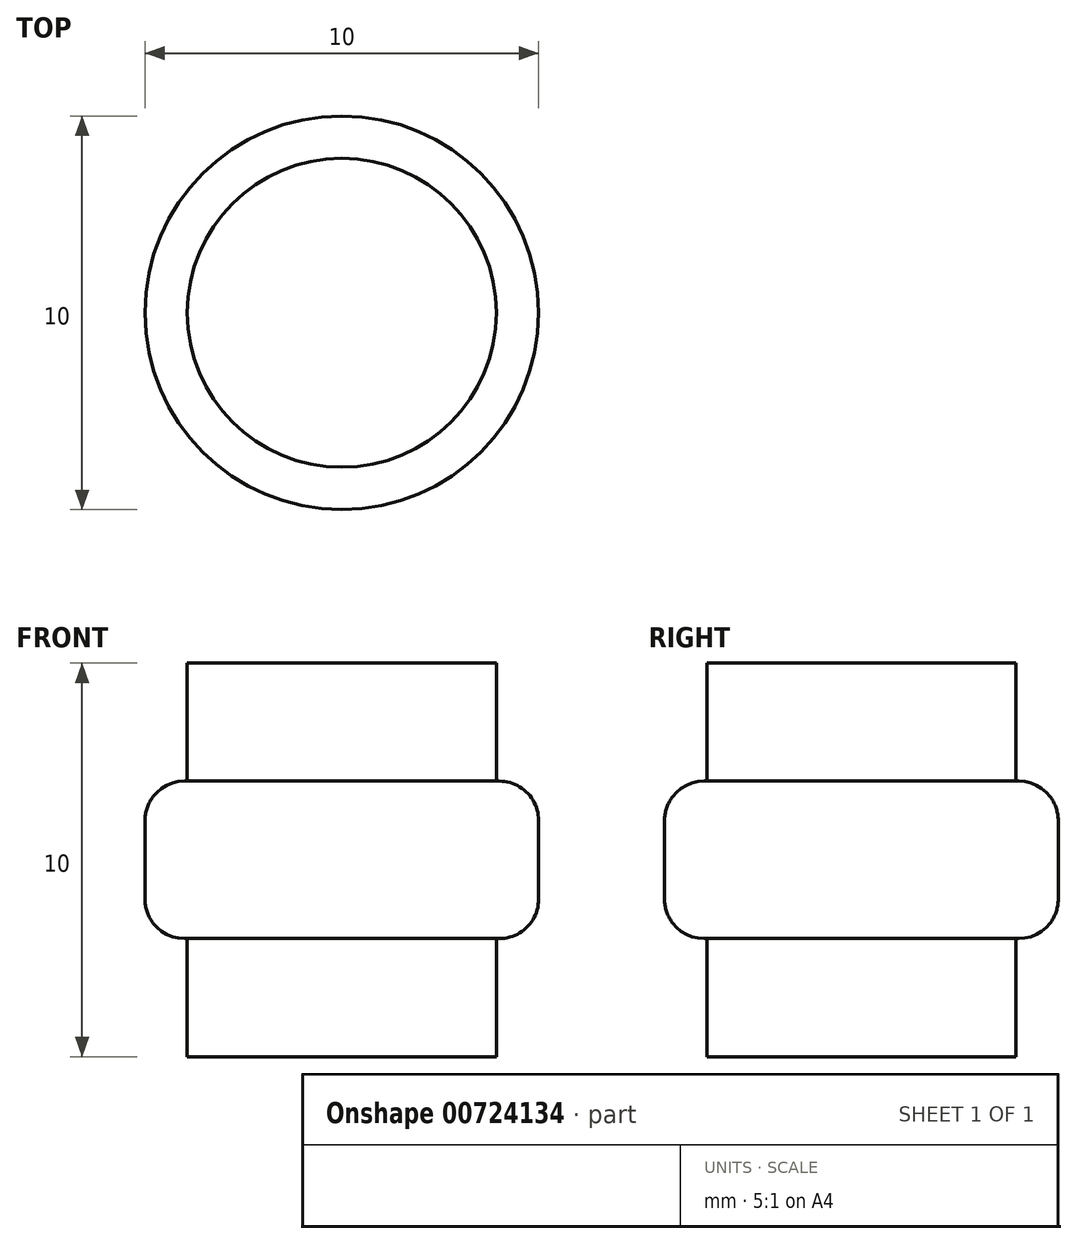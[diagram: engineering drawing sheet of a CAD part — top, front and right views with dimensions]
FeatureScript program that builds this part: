
annotation { "Feature Type Name" : "Feature", "Feature Type Description" : "" }
export const myFeature = defineFeature(function(context is Context, id is Id, definition is map)
    precondition{}
    {
        {
            var Q0;
            Q0=qCreatedBy(makeId("Top.planeOp"),FACE);
            var sketch = newSketch(context, id + "F0", { "sketchPlane" : qUnion([Q0])});
            skCircle(sketch, "E0", {"center": v(0, 0) * mm, "radius": 3.93 * mm});
            skCircle(sketch, "E1", {"center": v(0, 0) * mm, "radius": 5 * mm});
            skSolve(sketch);
        }
        {
            var Q0;
            Q0=makeQuery(id+"F0.imprint","IMPRINT",FACE,{"disambiguationData":[TD([[makeQuery(id+"F0.imprint","IMPRINT",EDGE,{"derivedFrom":sQuery(id+"F0.wireOp",EDGE,"E0")}),1.0]])]});
            extrude(context, id + "F1", {"entities" : qUnion([Q0]), "endBound" : BoundingType.SYMMETRIC, "oppositeDirection" : true, "depth" : 10 * mm, "offsetDistance" : 25 * mm});
        }
        {
            var Q0;
            Q0=makeQuery(id+"F0.imprint","IMPRINT",FACE,{"disambiguationData":[TD([[makeQuery(id+"F0.imprint","IMPRINT",EDGE,{"derivedFrom":sQuery(id+"F0.wireOp",EDGE,"E0")}),-1.0]])]});
            extrude(context, id + "F2", {"entities" : qUnion([Q0]), "operationType" : NewBodyOperationType.ADD, "endBound" : BoundingType.SYMMETRIC, "depth" : 4 * mm, "offsetDistance" : 25 * mm});
        }
        {
            var Q0;
            Q0=makeQuery(id+"F2.opExtrude","CAP_EDGE",EDGE,{"disambiguationData":[OSD([sQuery(id+"F0.wireOp",EDGE,"E1")])],"isStart":false});
            var Q1;
            Q1=makeQuery(id+"F2.opExtrude","CAP_EDGE",EDGE,{"disambiguationData":[OSD([sQuery(id+"F0.wireOp",EDGE,"E1")])],"isStart":true});
            fillet(context, id + "F3", {"entities" : qUnion([Q0, Q1]), "radius" : 1 * mm, "tangentPropagation" : true, "allowEdgeOverflow" : false});
        }
    });
